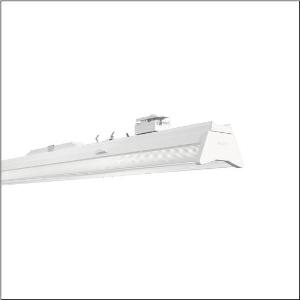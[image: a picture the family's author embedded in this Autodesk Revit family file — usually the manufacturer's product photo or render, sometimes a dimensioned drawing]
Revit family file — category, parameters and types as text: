
# Revit family: licross_r__21_performance_mo_52tm16dn4a5g_341e
name_source: partatom
category: Lighting Fixtures
units: mm (PartAtom-declared; Revit-internal decimal feet)

## family parameters
Cut with Voids When Loaded = No
Host = Face
Light Source = No
Part Type = Normal
Room Calculation Point = No
Round Connector Dimension = Use Diameter
Shared = No

## types (1)
- --- (1 x LED, 10840 lm, 62 W, 4000K)
    Apparent Load = 62 VA
    CIE Flux Codes = 66 88 96 79 100
    Color Rendering = 80
    Color Temperature = 4000K
    Default Elevation = 1800 mm
    Description = Licross® 21 Performance MO, luminaire insert, of sheet steel, galvanised, coil coated, white, length: 1.500mm, width: 120mm, height: 123mm, LED rated luminous flux: 10.840lm, light colour: 840, control gear: DALI 2, with plug, 5-pole, with phase selection, mains connection: 220..240V, AC, 50/60Hz, rated input power: 62W, halogen-free wiring, primary light control with lens, of plastic, primary optical cover: cover, of PMMA, light emission: direct/indirect distribution, primary light characteristic: symmetric, protection rating (complete): IP40, insulation class (complete): insulation class I (protective earthing), certification: CE, ENEC, UKCA, protection symbol: D if used in an environment without relevant dust loads with corresponding accessories, impact resistance: IK06, permissible ambient temperature for indoor applications: -25..+35°C, corresponds to IFS (International Featured Standards) requirements for safety and quality in the food industry, reducing of maximum allowable ambient temperature of 5°C with ceiling mounting, LABS conformity tested according to VDMA 24364:2018-05, packaging unit: 1 piece
    Height = 114 mm
    Lamp = 1 x LED
    Lamp Light Flux = 10840 lm
    Lamp Power = 62 W
    Lamp count = 1
    Length = 1500 mm
    Luminous efficacy = 175 lm/W
    Manufacturer = Siteco
    ModVariant = No
    Model = 52TM16DN4A5G
    Mounting Place = Ceiling
    Mounting Type = Pendant
    Number of Poles = 1
    OnlyDefault = Yes
    Power Factor = 1
    Product Name = Licross® 21 Performance MO
    Product group = luminaire insert
    ProductGroupID = 901
    Protection Class = Protection class I
    Protection Degree = IP 40
    RLX_Detail_Level = 1
    RLX_Emergency_Light_Flux = 0 lm
    RLX_Emergency_Type = 0
    RLX_Emergency_Type_DB = No
    RlxData = <blob elided: 34085 chars, md5=448d7e70>
    Socket = socket
    Standby Power = 0 W
    System Light Flux = 10840 lm
    System Power = 62 W
    Type Comments = factory setting: luminous flux: 100 % | dim-lin: 254 | 418 mA
    Type Image = l_1256138.jpg
    URL = http://relux.com
    VarID = @adj_078919
    Voltage = 0 V
    Weight = 0.00 kg
    Width = 120 mm

## geometry (parser evidence)
native form markers: Blend x4, Sweep x11
no freeform markers — native parametric forms only
